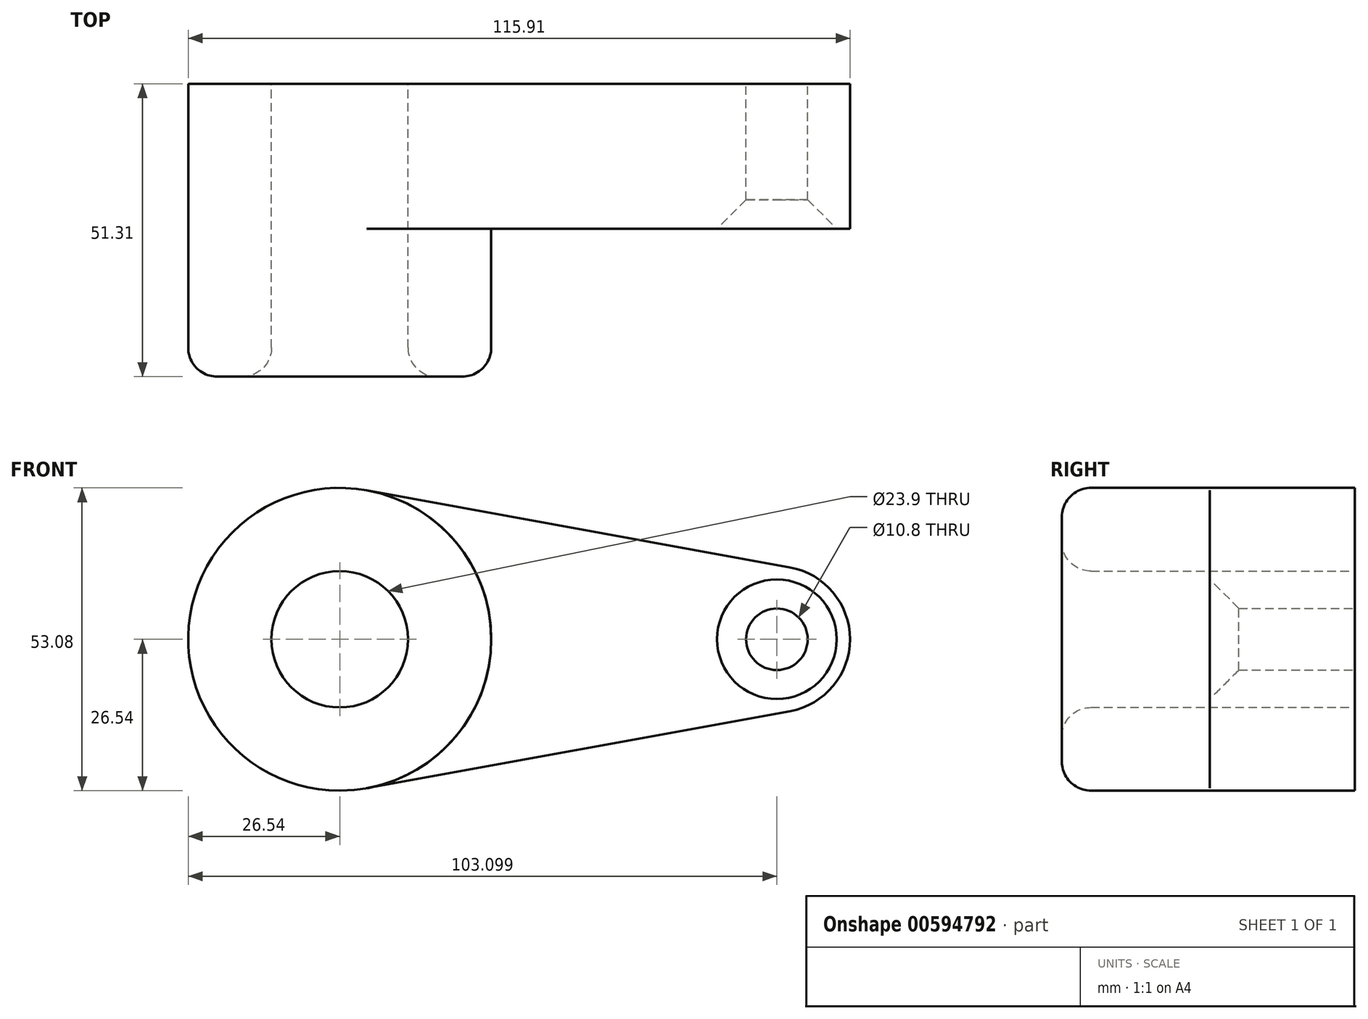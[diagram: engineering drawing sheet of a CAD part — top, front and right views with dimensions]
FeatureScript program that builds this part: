
annotation { "Feature Type Name" : "Feature", "Feature Type Description" : "" }
export const myFeature = defineFeature(function(context is Context, id is Id, definition is map)
    precondition{}
    {
        {
            var Q0;
            Q0=qCreatedBy(makeId("Front.planeOp"),FACE);
            var sketch = newSketch(context, id + "F0", { "sketchPlane" : qUnion([Q0])});
            skCircle(sketch, "E0", {"center": v(0, 0) * mm, "radius": 26.54 * mm});
            skCircle(sketch, "E1", {"center": v(76.56, 0) * mm, "radius": 12.8 * mm});
            skLineSegment(sketch, "E2", {"start": v(4.76, -26.1) * mm, "end": v(78.86, -12.6) * mm});
            skLineSegment(sketch, "E3", {"start": v(4.76, 26.1) * mm, "end": v(78.86, 12.6) * mm});
            skCircle(sketch, "E4", {"center": v(0, 0) * mm, "radius": 11.95 * mm});
            skCircle(sketch, "E5", {"center": v(76.56, 0) * mm, "radius": 5.4 * mm});
            skSolve(sketch);
        }
        {
            var Q0;
            Q0 = qSketchRegion(id + "F0", true);
            extrude(context, id + "F1", {"entities" : qUnion([Q0]), "depth" : 25.4 * mm, "offsetDistance" : 25.4 * mm});
        }
        {
            var Q0;
            Q0=makeQuery(id+"F0.imprint","IMPRINT",FACE,{"disambiguationData":[TD([[makeQuery(id+"F0.imprint","IMPRINT",EDGE,{"derivedFrom":sQuery(id+"F0.wireOp",EDGE,"E4")}),-1.0]])]});
            extrude(context, id + "F2", {"entities" : qUnion([Q0]), "operationType" : NewBodyOperationType.ADD, "depth" : 51.3 * mm, "offsetDistance" : 25.4 * mm});
        }
        {
            var Q0;
            Q0=makeQuery(id+"F2.opExtrude","CAP_FACE",FACE,{"disambiguationData":[OSD([sQuery(id+"F0.wireOp",EDGE,"E0"),sQuery(id+"F0.wireOp",EDGE,"E4")])],"isStart":false});
            fillet(context, id + "F3", {"entities" : qUnion([Q0]), "radius" : 5.08 * mm, "tangentPropagation" : true, "allowEdgeOverflow" : false});
        }
        {
            var Q0;
            Q0=makeQuery(id+"F1.opExtrude","CAP_EDGE",EDGE,{"disambiguationData":[OSD([sQuery(id+"F0.wireOp",EDGE,"E5")])],"isStart":false});
            chamfer(context, id + "F4", {"entities" : qUnion([Q0]), "width" : 5.08 * mm, "tangentPropagation" : true});
        }
    });
